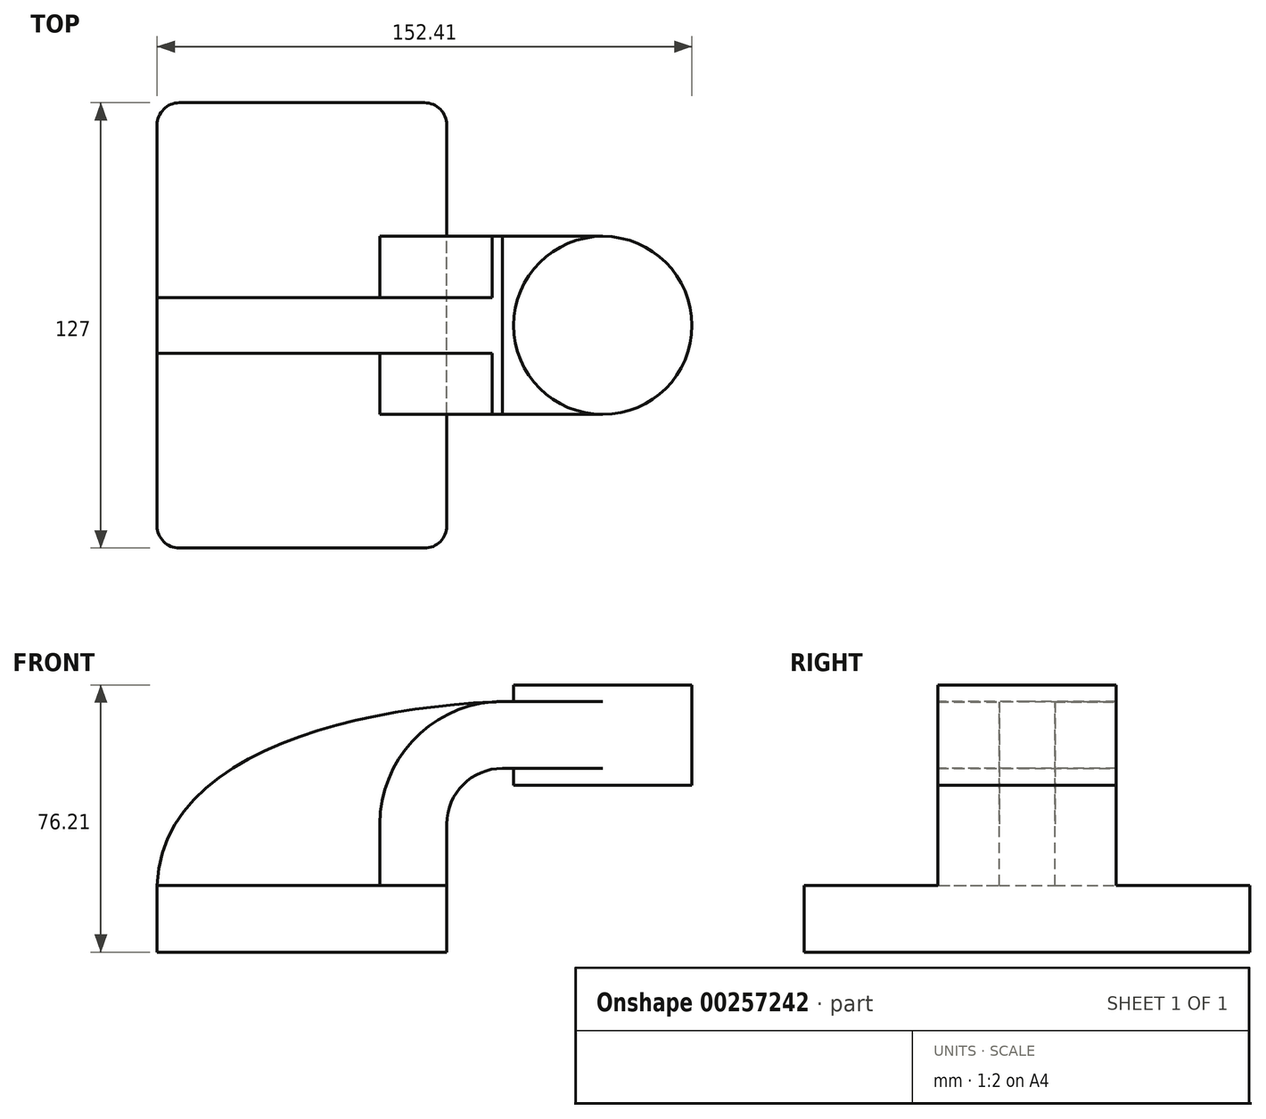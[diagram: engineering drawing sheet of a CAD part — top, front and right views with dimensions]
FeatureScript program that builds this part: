
annotation { "Feature Type Name" : "Feature", "Feature Type Description" : "" }
export const myFeature = defineFeature(function(context is Context, id is Id, definition is map)
    precondition{}
    {
        {
            var Q0;
            Q0=qCreatedBy(makeId("Front.planeOp"),FACE);
            var sketch = newSketch(context, id + "F0", { "sketchPlane" : qUnion([Q0])});
            skLineSegment(sketch, "E0.bottom", {"start": v(41.27, 9.53) * mm, "end": v(-41.27, 9.53) * mm});
            skLineSegment(sketch, "E0.top", {"start": v(41.28, -9.52) * mm, "end": v(-41.27, -9.52) * mm});
            skLineSegment(sketch, "E0.left", {"start": v(41.27, 9.53) * mm, "end": v(41.28, -9.52) * mm});
            skLineSegment(sketch, "E0.right", {"start": v(-41.27, 9.53) * mm, "end": v(-41.27, -9.52) * mm});
            skPoint(sketch, "E0.middle", {"position": v(0, 0) * mm});
            skLineSegment(sketch, "E1.bottom", {"start": v(60.32, 66.68) * mm, "end": v(111.12, 66.68) * mm});
            skLineSegment(sketch, "E1.top", {"start": v(60.32, 38.1) * mm, "end": v(111.12, 38.1) * mm});
            skLineSegment(sketch, "E1.left", {"start": v(60.32, 66.68) * mm, "end": v(60.32, 38.1) * mm});
            skLineSegment(sketch, "E1.right", {"start": v(111.12, 66.68) * mm, "end": v(111.12, 38.1) * mm});
            skPoint(sketch, "E1.middle", {"position": v(85.72, 52.39) * mm});
            skLineSegment(sketch, "E2", {"start": v(41.27, 9.53) * mm, "end": v(41.27, 27) * mm});
            skArc(sketch, "E3", {"start": v(41.27, 27) * mm, "mid": v(45.92, 38.23) * mm, "end": v(57.15, 42.88) * mm});
            skLineSegment(sketch, "E4", {"start": v(57.15, 42.88) * mm, "end": v(85.72, 42.88) * mm});
            skLineSegment(sketch, "E5.0", {"start": v(57.15, 61.93) * mm, "end": v(85.72, 61.93) * mm});
            skArc(sketch, "E5.1", {"start": v(22.22, 27) * mm, "mid": v(32.45, 51.7) * mm, "end": v(57.15, 61.93) * mm});
            skLineSegment(sketch, "E5.2", {"start": v(22.22, 9.53) * mm, "end": v(22.22, 27) * mm});
            skFitSpline(sketch, "E6", {"points": [v(-41.28, 9.53) * mm, v(57.15, 61.93) * mm], "startDerivative": vector(4.03, 114.73) * mm, "endDerivative": vector(122.63, 4.4) * mm});
            skLineSegment(sketch, "E7", {"start": v(85.72, 38.1) * mm, "end": v(85.72, 66.68) * mm});
            skSolve(sketch);
        }
        {
            var Q0;
            Q0=makeQuery(id+"F0.imprint","IMPRINT",FACE,{"disambiguationData":[TD([[makeQuery(id+"F0.imprint","IMPRINT",EDGE,{"derivedFrom":sQuery(id+"F0.wireOp",EDGE,"E0.top")}),-1.0]])]});
            extrude(context, id + "F1", {"entities" : qUnion([Q0]), "endBound" : BoundingType.SYMMETRIC, "depth" : 127 * mm});
        }
        {
            var Q0;
            {var subQ1=sQuery(id+"F0.wireOp",EDGE,"E2");Q0=makeQuery(id+"F0.imprint","IMPRINT",FACE,{"disambiguationData":[TD([[makeQuery(id+"F0.imprint","IMPRINT",EDGE,{"derivedFrom":subQ1}),1.0]])]});}
            extrude(context, id + "F2", {"entities" : qUnion([Q0]), "operationType" : NewBodyOperationType.ADD, "endBound" : BoundingType.SYMMETRIC, "depth" : 50.8 * mm});
        }
        {
            var Q0;
            {var subQ3=sQuery(id+"F0.wireOp",EDGE,"E5.2");Q0=makeQuery(id+"F0.imprint","IMPRINT",FACE,{"disambiguationData":[TD([[makeQuery(id+"F0.imprint","IMPRINT",EDGE,{"derivedFrom":subQ3}),1.0]])]});}
            extrude(context, id + "F3", {"entities" : qUnion([Q0]), "operationType" : NewBodyOperationType.ADD, "endBound" : BoundingType.SYMMETRIC, "depth" : 15.88 * mm});
        }
        {
            var Q0;
            {var subQ0=sQuery(id+"F0.wireOp",EDGE,"E5.0");var subQ1=sQuery(id+"F0.wireOp",EDGE,"E1.left");var subQ2=makeQuery(id+"F0.imprint","INTERSECT",VERTEX,{"derivedFrom":[subQ1,subQ0]});Q0=makeQuery(id+"F0.imprint","IMPRINT",FACE,{"disambiguationData":[TD([[makeQuery(id+"F0.imprint","IMPRINT",EDGE,{"disambiguationData":[TD([[subQ2,-1.0]])],"derivedFrom":subQ1}),1.0]])]});}
            extrude(context, id + "F4", {"entities" : qUnion([Q0]), "operationType" : NewBodyOperationType.ADD, "endBound" : BoundingType.SYMMETRIC, "depth" : 50.8 * mm});
        }
        {
            var Q0;
            {var subQ0=sQuery(id+"F0.wireOp",EDGE,"E1.right");Q0=makeQuery(id+"F0.imprint","IMPRINT",FACE,{"disambiguationData":[TD([[makeQuery(id+"F0.imprint","IMPRINT",EDGE,{"derivedFrom":subQ0}),-1.0]])]});}
            var Q1;
            Q1=sQuery(id+"F0.wireOp",EDGE,"E7");
            revolve(context, id + "F5", {"operationType" : NewBodyOperationType.ADD, "entities" : qUnion([Q0]), "axis" : qUnion([Q1]), "revolveType" : RevolveType.FULL});
        }
        {
            var Q0;
            Q0=makeQuery(id+"F1.opExtrude","CAP_EDGE",EDGE,{"disambiguationData":[OSD([sQuery(id+"F0.wireOp",EDGE,"E0.left")])],"isStart":false});
            var Q1;
            Q1=makeQuery(id+"F1.opExtrude","CAP_EDGE",EDGE,{"disambiguationData":[OSD([sQuery(id+"F0.wireOp",EDGE,"E0.right")])],"isStart":false});
            var Q2;
            Q2=makeQuery(id+"F1.opExtrude","CAP_EDGE",EDGE,{"disambiguationData":[OSD([sQuery(id+"F0.wireOp",EDGE,"E0.right")])],"isStart":true});
            var Q3;
            Q3=makeQuery(id+"F1.opExtrude","CAP_EDGE",EDGE,{"disambiguationData":[OSD([sQuery(id+"F0.wireOp",EDGE,"E0.left")])],"isStart":true});
            fillet(context, id + "F6", {"entities" : qUnion([Q0, Q1, Q2, Q3]), "radius" : 6.35 * mm, "tangentPropagation" : true, "allowEdgeOverflow" : false});
        }
    });
